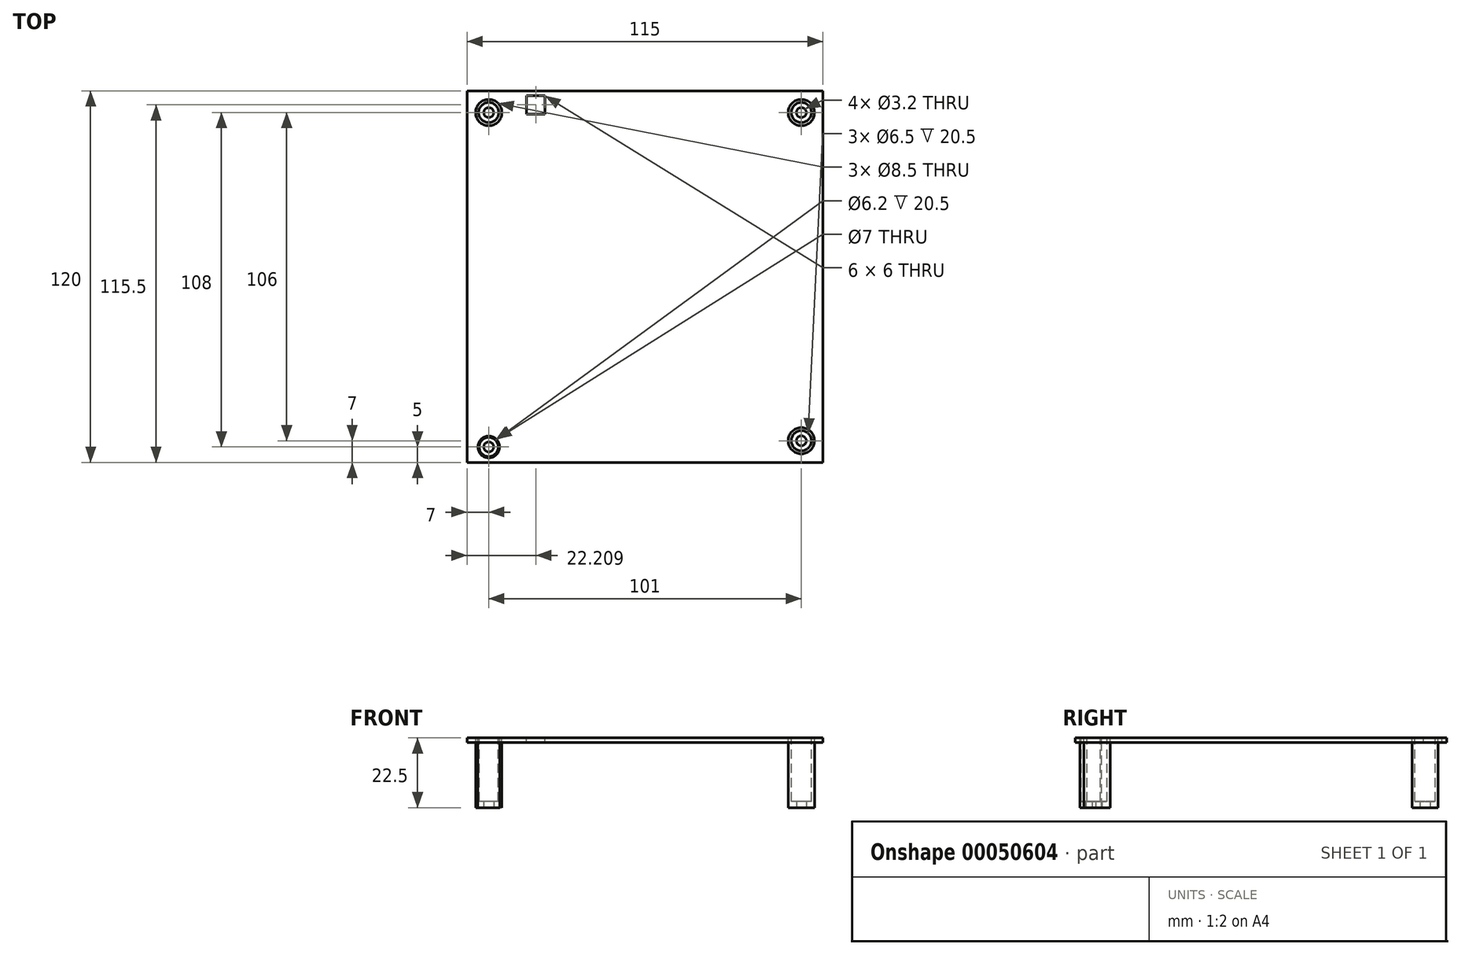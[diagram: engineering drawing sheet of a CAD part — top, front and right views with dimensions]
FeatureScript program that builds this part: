
annotation { "Feature Type Name" : "Feature", "Feature Type Description" : "" }
export const myFeature = defineFeature(function(context is Context, id is Id, definition is map)
    precondition{}
    {
        {
            var Q0;
            Q0=qCreatedBy(makeId("Top.planeOp"),FACE);
            var sketch = newSketch(context, id + "F0", { "sketchPlane" : qUnion([Q0])});
            skLineSegment(sketch, "E0.bottom", {"start": v(-52.5, 65) * mm, "end": v(62.5, 65) * mm});
            skLineSegment(sketch, "E0.top", {"start": v(-52.5, -55) * mm, "end": v(62.5, -55) * mm});
            skLineSegment(sketch, "E0.left", {"start": v(-52.5, 65) * mm, "end": v(-52.5, -55) * mm});
            skLineSegment(sketch, "E0.right", {"start": v(62.5, 65) * mm, "end": v(62.5, -55) * mm});
            skLineSegment(sketch, "E1.rect.bottom", {"start": v(-27.3, 57.5) * mm, "end": v(-33.3, 57.5) * mm});
            skLineSegment(sketch, "E1.rect.top", {"start": v(-27.3, 63.5) * mm, "end": v(-33.3, 63.5) * mm});
            skLineSegment(sketch, "E1.rect.left", {"start": v(-27.3, 57.5) * mm, "end": v(-27.3, 63.5) * mm});
            skLineSegment(sketch, "E1.rect.right", {"start": v(-33.3, 57.5) * mm, "end": v(-33.3, 63.5) * mm});
            skPoint(sketch, "E1.rect.middle", {"position": v(-30.3, 60.5) * mm});
            skCircle(sketch, "E2", {"center": v(-45.5, 58) * mm, "radius": 4.25 * mm});
            skCircle(sketch, "E3", {"center": v(55.5, 58) * mm, "radius": 4.25 * mm});
            skCircle(sketch, "E4", {"center": v(55.5, -48) * mm, "radius": 4.25 * mm});
            skCircle(sketch, "E5", {"center": v(-45.5, -50) * mm, "radius": 3.5 * mm});
            skSolve(sketch);
        }
        {
            var Q0;
            Q0=makeQuery(id+"F0.imprint","IMPRINT",FACE,{"disambiguationData":[TD([[makeQuery(id+"F0.imprint","IMPRINT",EDGE,{"derivedFrom":sQuery(id+"F0.wireOp",EDGE,"E0.bottom")}),-1.0]])]});
            extrude(context, id + "F1", {"entities" : qUnion([Q0]), "oppositeDirection" : true, "depth" : 1.5 * mm});
        }
        {
            var Q0;
            Q0=makeQuery(id+"F0.imprint","IMPRINT",FACE,{"disambiguationData":[TD([[makeQuery(id+"F0.imprint","IMPRINT",EDGE,{"derivedFrom":sQuery(id+"F0.wireOp",EDGE,"E2")}),1.0]])]});
            var Q1;
            Q1=makeQuery(id+"F0.imprint","IMPRINT",FACE,{"disambiguationData":[TD([[makeQuery(id+"F0.imprint","IMPRINT",EDGE,{"derivedFrom":sQuery(id+"F0.wireOp",EDGE,"E3")}),1.0]])]});
            var Q2;
            Q2=makeQuery(id+"F0.imprint","IMPRINT",FACE,{"disambiguationData":[TD([[makeQuery(id+"F0.imprint","IMPRINT",EDGE,{"derivedFrom":sQuery(id+"F0.wireOp",EDGE,"E5")}),1.0]])]});
            var Q3;
            Q3=makeQuery(id+"F0.imprint","IMPRINT",FACE,{"disambiguationData":[TD([[makeQuery(id+"F0.imprint","IMPRINT",EDGE,{"derivedFrom":sQuery(id+"F0.wireOp",EDGE,"E4")}),1.0]])]});
            extrude(context, id + "F2", {"entities" : qUnion([Q0, Q1, Q2, Q3]), "oppositeDirection" : true, "depth" : 22.5 * mm});
        }
        {
            var Q0;
            Q0=makeQuery(id+"F2.opExtrude","CAP_FACE",FACE,{"disambiguationData":[OSD([sQuery(id+"F0.wireOp",EDGE,"E3")])],"isStart":true});
            var sketch = newSketch(context, id + "F3", { "sketchPlane" : qUnion([Q0])});
            skCircle(sketch, "E6", {"center": v(55.5, 58) * mm, "radius": 3.25 * mm});
            skSolve(sketch);
        }
        {
            var Q0;
            Q0=makeQuery(id+"F3.imprint","IMPRINT",FACE,{"disambiguationData":[TD([[makeQuery(id+"F3.imprint","IMPRINT",EDGE,{"derivedFrom":sQuery(id+"F3.wireOp",EDGE,"E6")}),1.0]])]});
            extrude(context, id + "F4", {"entities" : qUnion([Q0]), "operationType" : NewBodyOperationType.REMOVE, "oppositeDirection" : true, "depth" : 20.5 * mm});
        }
        {
            var Q0;
            Q0=makeQuery(id+"F2.opExtrude","CAP_FACE",FACE,{"disambiguationData":[OSD([sQuery(id+"F0.wireOp",EDGE,"E2")])],"isStart":true});
            var sketch = newSketch(context, id + "F5", { "sketchPlane" : qUnion([Q0])});
            skCircle(sketch, "E7", {"center": v(-45.5, 58) * mm, "radius": 3.25 * mm});
            skSolve(sketch);
        }
        {
            var Q0;
            Q0=makeQuery(id+"F5.imprint","IMPRINT",FACE,{"disambiguationData":[TD([[makeQuery(id+"F5.imprint","IMPRINT",EDGE,{"derivedFrom":sQuery(id+"F5.wireOp",EDGE,"E7")}),1.0]])]});
            extrude(context, id + "F6", {"entities" : qUnion([Q0]), "operationType" : NewBodyOperationType.REMOVE, "oppositeDirection" : true, "depth" : 20.5 * mm});
        }
        {
            var Q0;
            Q0=makeQuery(id+"F2.opExtrude","CAP_FACE",FACE,{"disambiguationData":[OSD([sQuery(id+"F0.wireOp",EDGE,"E5")])],"isStart":true});
            var sketch = newSketch(context, id + "F7", { "sketchPlane" : qUnion([Q0])});
            skCircle(sketch, "E8", {"center": v(-45.5, -50) * mm, "radius": 3.1 * mm});
            skSolve(sketch);
        }
        {
            var Q0;
            Q0=makeQuery(id+"F7.imprint","IMPRINT",FACE,{"disambiguationData":[TD([[makeQuery(id+"F7.imprint","IMPRINT",EDGE,{"derivedFrom":sQuery(id+"F7.wireOp",EDGE,"E8")}),1.0]])]});
            extrude(context, id + "F8", {"entities" : qUnion([Q0]), "operationType" : NewBodyOperationType.REMOVE, "oppositeDirection" : true, "depth" : 20.5 * mm});
        }
        {
            var Q0;
            Q0=makeQuery(id+"F2.opExtrude","CAP_FACE",FACE,{"disambiguationData":[OSD([sQuery(id+"F0.wireOp",EDGE,"E4")])],"isStart":true});
            var sketch = newSketch(context, id + "F9", { "sketchPlane" : qUnion([Q0])});
            skCircle(sketch, "E9", {"center": v(55.5, -48) * mm, "radius": 3.25 * mm});
            skSolve(sketch);
        }
        {
            var Q0;
            Q0=makeQuery(id+"F9.imprint","IMPRINT",FACE,{"disambiguationData":[TD([[makeQuery(id+"F9.imprint","IMPRINT",EDGE,{"derivedFrom":sQuery(id+"F9.wireOp",EDGE,"E9")}),1.0]])]});
            extrude(context, id + "F10", {"entities" : qUnion([Q0]), "operationType" : NewBodyOperationType.REMOVE, "oppositeDirection" : true, "depth" : 20.5 * mm});
        }
        {
            var Q0;
            Q0=makeQuery(id+"F2.opExtrude","CAP_FACE",FACE,{"disambiguationData":[OSD([sQuery(id+"F0.wireOp",EDGE,"E5")])],"isStart":false});
            var sketch = newSketch(context, id + "F11", { "sketchPlane" : qUnion([Q0])});
            skCircle(sketch, "E10", {"center": v(-45.5, 50) * mm, "radius": 1.6 * mm});
            skSolve(sketch);
        }
        {
            var Q0;
            Q0=makeQuery(id+"F11.imprint","IMPRINT",FACE,{"disambiguationData":[TD([[makeQuery(id+"F11.imprint","IMPRINT",EDGE,{"derivedFrom":sQuery(id+"F11.wireOp",EDGE,"E10")}),1.0]])]});
            extrude(context, id + "F12", {"entities" : qUnion([Q0]), "operationType" : NewBodyOperationType.REMOVE, "oppositeDirection" : true, "depth" : 2.5 * mm});
        }
        {
            var Q0;
            Q0=makeQuery(id+"F2.opExtrude","CAP_FACE",FACE,{"disambiguationData":[OSD([sQuery(id+"F0.wireOp",EDGE,"E2")])],"isStart":false});
            var sketch = newSketch(context, id + "F13", { "sketchPlane" : qUnion([Q0])});
            skCircle(sketch, "E11", {"center": v(-45.5, -58) * mm, "radius": 1.6 * mm});
            skSolve(sketch);
        }
        {
            var Q0;
            Q0=makeQuery(id+"F13.imprint","IMPRINT",FACE,{"disambiguationData":[TD([[makeQuery(id+"F13.imprint","IMPRINT",EDGE,{"derivedFrom":sQuery(id+"F13.wireOp",EDGE,"E11")}),1.0]])]});
            extrude(context, id + "F14", {"entities" : qUnion([Q0]), "operationType" : NewBodyOperationType.REMOVE, "oppositeDirection" : true, "depth" : 2.5 * mm});
        }
        {
            var Q0;
            Q0=makeQuery(id+"F2.opExtrude","CAP_FACE",FACE,{"disambiguationData":[OSD([sQuery(id+"F0.wireOp",EDGE,"E3")])],"isStart":false});
            var sketch = newSketch(context, id + "F15", { "sketchPlane" : qUnion([Q0])});
            skCircle(sketch, "E12", {"center": v(55.5, -58) * mm, "radius": 1.6 * mm});
            skSolve(sketch);
        }
        {
            var Q0;
            Q0=makeQuery(id+"F15.imprint","IMPRINT",FACE,{"disambiguationData":[TD([[makeQuery(id+"F15.imprint","IMPRINT",EDGE,{"derivedFrom":sQuery(id+"F15.wireOp",EDGE,"E12")}),1.0]])]});
            extrude(context, id + "F16", {"entities" : qUnion([Q0]), "operationType" : NewBodyOperationType.REMOVE, "oppositeDirection" : true, "depth" : 2.5 * mm});
        }
        {
            var Q0;
            Q0=makeQuery(id+"F2.opExtrude","CAP_FACE",FACE,{"disambiguationData":[OSD([sQuery(id+"F0.wireOp",EDGE,"E4")])],"isStart":false});
            var sketch = newSketch(context, id + "F17", { "sketchPlane" : qUnion([Q0])});
            skCircle(sketch, "E13", {"center": v(55.5, 48) * mm, "radius": 1.6 * mm});
            skSolve(sketch);
        }
        {
            var Q0;
            Q0=makeQuery(id+"F17.imprint","IMPRINT",FACE,{"disambiguationData":[TD([[makeQuery(id+"F17.imprint","IMPRINT",EDGE,{"derivedFrom":sQuery(id+"F17.wireOp",EDGE,"E13")}),1.0]])]});
            extrude(context, id + "F18", {"entities" : qUnion([Q0]), "operationType" : NewBodyOperationType.REMOVE, "oppositeDirection" : true, "depth" : 2.5 * mm});
        }
    });
